# Revit family: BVN-BPR
name_source: partatom
category: Generic Models
units: mm (PartAtom-declared; Revit-internal decimal feet)

## family parameters
Can host rebar = No
Cut with Voids When Loaded = No
Host = Face
Part Type = Normal
Room Calculation Point = No
Round Connector Dimension = Use Diameter
Shared = No

## types (2) — shared parameters
C = 20 mm  [stored 0.0656168 ft]
Default Elevation = 1219 mm
Description = Plastic Fan
E = 128 mm
F = 100 mm  [stored 0.328084 ft]
Frequency = 50 Hz
Insulation Class = B
Manufacturer = BVN
Model = BPR
Pieces In Box = 6
Protection Class = 20
URL = http://www.bahcivanmotor.com.tr
Voltage = 230 V
x' = 74 mm

## per-type parameters (varying)
| type | A | Air Flow | B | Capacitor(uF) | Current | D | D' | G | H | Material | Power | Sound Pressure Llevel dB(A) | Speed (d/d) | Weight |
| BPR 1012 | 240 mm | 120 m³/h | 220 mm | 0.4 | 1 A | 38 mm | -38 mm | 101 mm | 200 mm  [stored 0.656168 ft] | Stainless Steel | 22 W | 28 | 1050 | 1.90 kg |
| BPR 1015 | 264 mm  [stored 0.866142 ft] | 150 m³/h | 240 mm | 0.12 | 0 A | 40 mm  [stored 0.131234 ft] | -40 mm  [stored -0.131234 ft] | 114 mm  [stored 0.374016 ft] | 224 mm  [stored 0.734908 ft] | <By Category> | 28 W | 32 | 1550 | 2.10 kg |

note: [stored X ft] marks values corroborated as IEEE doubles in the binary element streams (Revit-internal decimal feet)

## geometry (parser evidence)
native form markers: Sweep x2
no freeform markers — native parametric forms only
